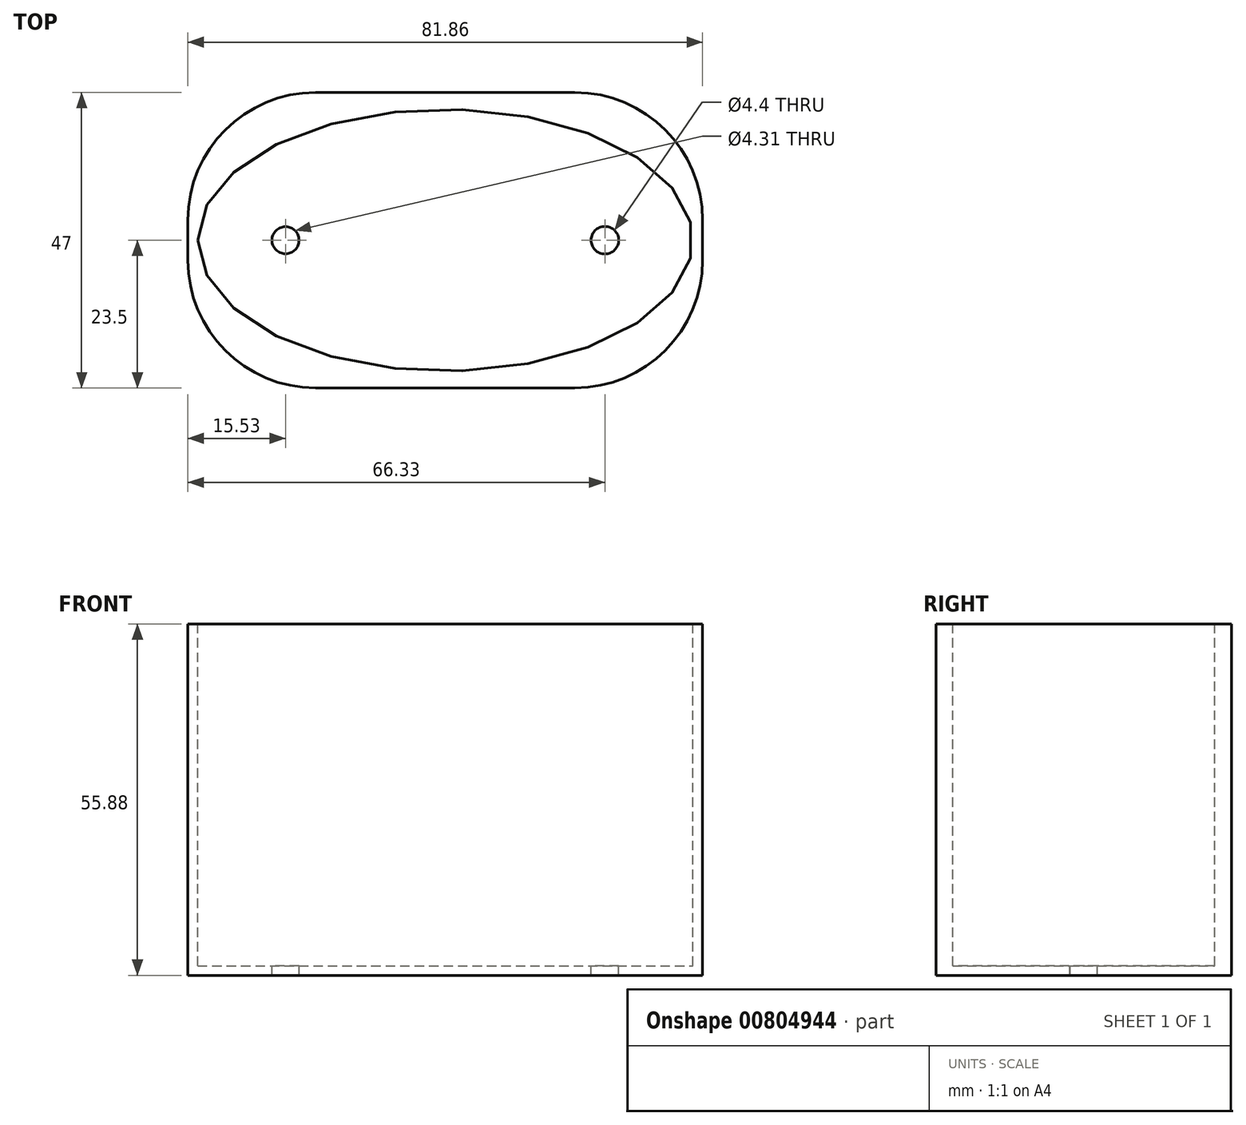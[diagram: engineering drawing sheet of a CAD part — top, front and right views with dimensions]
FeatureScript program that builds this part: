
annotation { "Feature Type Name" : "Feature", "Feature Type Description" : "" }
export const myFeature = defineFeature(function(context is Context, id is Id, definition is map)
    precondition{}
    {
        {
            var Q0;
            Q0=qCreatedBy(makeId("Top.planeOp"),FACE);
            var sketch = newSketch(context, id + "F0", { "sketchPlane" : qUnion([Q0])});
            skLineSegment(sketch, "E0.bottom", {"start": v(-20.61, 23.5) * mm, "end": v(20.61, 23.5) * mm});
            skLineSegment(sketch, "E0.top", {"start": v(-20.61, -23.5) * mm, "end": v(20.61, -23.5) * mm});
            skLineSegment(sketch, "E0.left", {"start": v(-40.93, 3.17) * mm, "end": v(-40.93, -3.18) * mm});
            skLineSegment(sketch, "E0.right", {"start": v(40.93, 3.17) * mm, "end": v(40.93, -3.17) * mm});
            skPoint(sketch, "E0.middle", {"position": v(0, 0) * mm});
            skPoint(sketch, "E1.visualSharp", {"position": v(-40.93, 23.5) * mm});
            skArc(sketch, "E1.filletArc", {"start": v(-20.61, 23.5) * mm, "mid": v(-34.98, 17.54) * mm, "end": v(-40.93, 3.17) * mm});
            skPoint(sketch, "E2.visualSharp", {"position": v(-40.93, -23.5) * mm});
            skArc(sketch, "E2.filletArc", {"start": v(-40.93, -3.18) * mm, "mid": v(-34.98, -17.54) * mm, "end": v(-20.61, -23.5) * mm});
            skPoint(sketch, "E3.visualSharp", {"position": v(40.93, -23.5) * mm});
            skArc(sketch, "E3.filletArc", {"start": v(20.61, -23.5) * mm, "mid": v(34.98, -17.54) * mm, "end": v(40.93, -3.18) * mm});
            skPoint(sketch, "E4.visualSharp", {"position": v(40.93, 23.5) * mm});
            skArc(sketch, "E4.filletArc", {"start": v(40.93, 3.17) * mm, "mid": v(34.98, 17.54) * mm, "end": v(20.61, 23.5) * mm});
            skSolve(sketch);
        }
        {
            var Q0;
            Q0 = qSketchRegion(id + "F0", true);
            extrude(context, id + "F1", {"entities" : qUnion([Q0]), "depth" : 55.88 * mm, "offsetDistance" : 25.4 * mm});
        }
        {
            var Q0;
            Q0=makeQuery(id+"F1.opExtrude","CAP_FACE",FACE,{"disambiguationData":[OSD([sQuery(id+"F0.wireOp",EDGE,"E0.bottom"),sQuery(id+"F0.wireOp",EDGE,"E0.top"),sQuery(id+"F0.wireOp",EDGE,"E0.left"),sQuery(id+"F0.wireOp",EDGE,"E0.right"),sQuery(id+"F0.wireOp",EDGE,"E1.filletArc"),sQuery(id+"F0.wireOp",EDGE,"E2.filletArc"),sQuery(id+"F0.wireOp",EDGE,"E3.filletArc"),sQuery(id+"F0.wireOp",EDGE,"E4.filletArc")])],"isStart":false});
            var sketch = newSketch(context, id + "F2", { "sketchPlane" : qUnion([Q0])});
            skEllipse(sketch, "E5", {"center": v(0, 0) * mm, "majorRadius": 39.37 * mm, "minorRadius": 20.83 * mm, "majorAxis": v(-1, 0)});
            skSolve(sketch);
        }
        {
            var Q0;
            Q0 = qSketchRegion(id + "F2", true);
            var Q1;
            Q1=makeQuery(id+"F1.opExtrude","CAP_FACE",FACE,{"disambiguationData":[OSD([sQuery(id+"F0.wireOp",EDGE,"E0.bottom"),sQuery(id+"F0.wireOp",EDGE,"E0.top"),sQuery(id+"F0.wireOp",EDGE,"E0.left"),sQuery(id+"F0.wireOp",EDGE,"E0.right"),sQuery(id+"F0.wireOp",EDGE,"E1.filletArc"),sQuery(id+"F0.wireOp",EDGE,"E2.filletArc"),sQuery(id+"F0.wireOp",EDGE,"E3.filletArc"),sQuery(id+"F0.wireOp",EDGE,"E4.filletArc")])],"isStart":true});
            extrude(context, id + "F3", {"entities" : qUnion([Q0]), "operationType" : NewBodyOperationType.REMOVE, "endBound" : BoundingType.UP_TO_SURFACE, "oppositeDirection" : true, "depth" : 25.4 * mm, "endBoundEntityFace" : qUnion([Q1]), "hasOffset" : true, "offsetDistance" : 1.5 * mm});
        }
        {
            var Q0;
            Q0=makeQuery(id+"F3.boolean.opBoolean","COPY",FACE,{"derivedFrom":makeQuery(id+"F3.opExtrude","CAP_FACE",FACE,{"disambiguationData":[OSD([sQuery(id+"F2.wireOp",EDGE,"E5")])],"isStart":false})});
            var sketch = newSketch(context, id + "F4", { "sketchPlane" : qUnion([Q0])});
            skCircle(sketch, "E6", {"center": v(-25.4, 0) * mm, "radius": 2.16 * mm});
            skCircle(sketch, "E7", {"center": v(25.4, 0) * mm, "radius": 2.2 * mm});
            skSolve(sketch);
        }
        {
            var Q0;
            Q0 = qSketchRegion(id + "F4", true);
            extrude(context, id + "F5", {"entities" : qUnion([Q0]), "operationType" : NewBodyOperationType.REMOVE, "endBound" : BoundingType.THROUGH_ALL, "oppositeDirection" : true, "depth" : 25.4 * mm, "offsetDistance" : 25.4 * mm});
        }
    });
